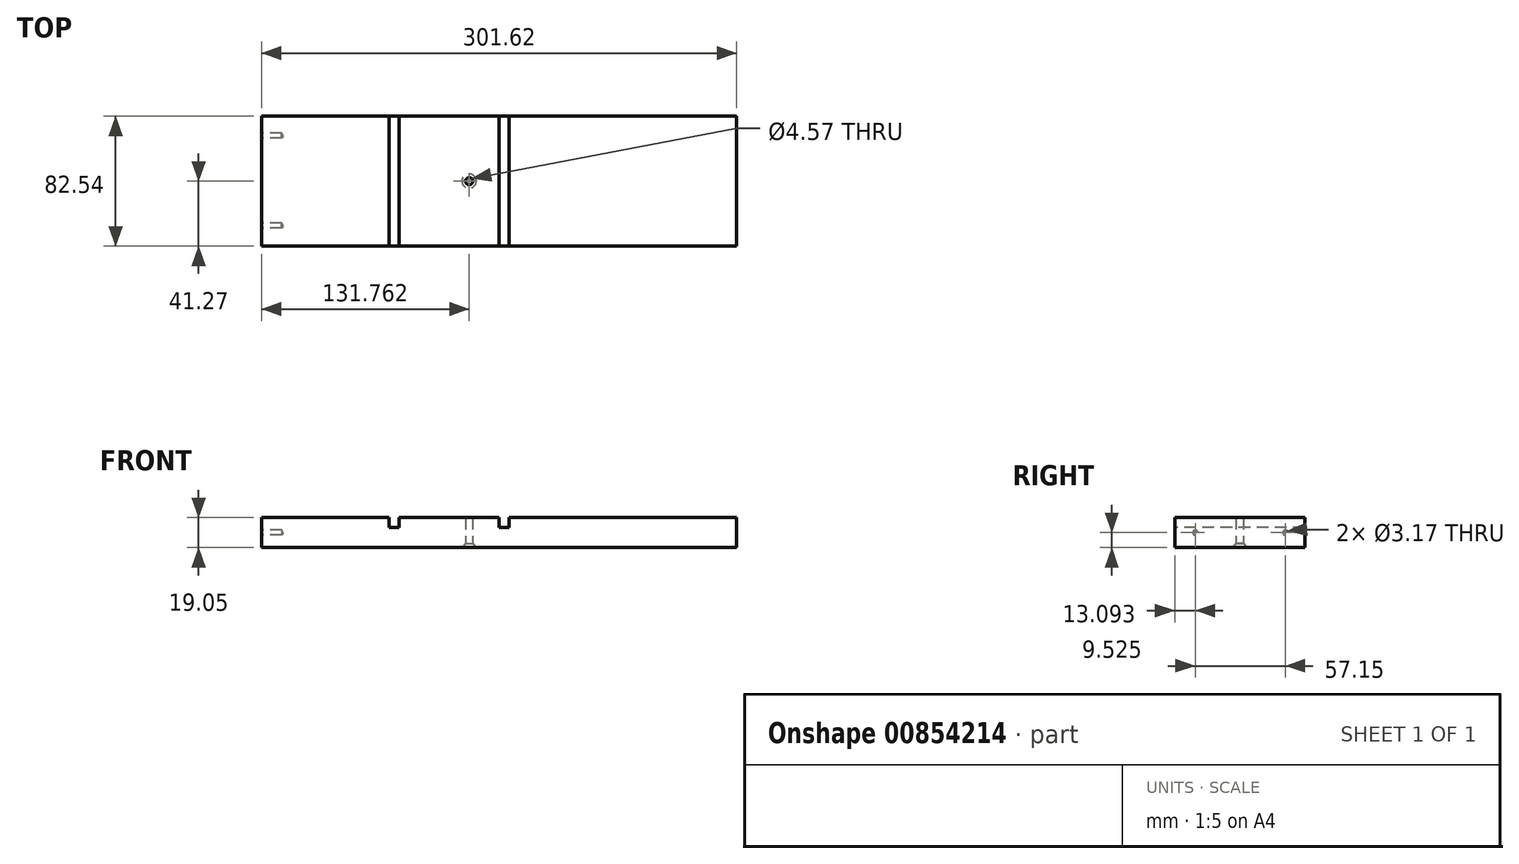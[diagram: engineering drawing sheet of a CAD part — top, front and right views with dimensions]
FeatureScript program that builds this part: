
annotation { "Feature Type Name" : "Feature", "Feature Type Description" : "" }
export const myFeature = defineFeature(function(context is Context, id is Id, definition is map)
    precondition{}
    {
        {
            var Q0;
            Q0=qCreatedBy(makeId("Top.planeOp"),FACE);
            var sketch = newSketch(context, id + "F0", { "sketchPlane" : qUnion([Q0])});
            skLineSegment(sketch, "E0", {"start": v(-114.3, 41.27) * mm, "end": v(187.33, 41.28) * mm});
            skLineSegment(sketch, "E1", {"start": v(-114.3, 41.27) * mm, "end": v(-114.3, -41.28) * mm});
            skLineSegment(sketch, "E2", {"start": v(-114.3, -41.27) * mm, "end": v(187.32, -41.27) * mm});
            skLineSegment(sketch, "E3", {"start": v(187.32, -41.28) * mm, "end": v(187.32, 41.28) * mm});
            skLineSegment(sketch, "E4", {"start": v(187.33, 41.28) * mm, "end": v(187.32, 41.28) * mm});
            skSolve(sketch);
        }
        {
            var Q0;
            Q0=makeQuery(id+"F0.imprint","IMPRINT",FACE,{"disambiguationData":[TD([[makeQuery(id+"F0.imprint","IMPRINT",EDGE,{"derivedFrom":sQuery(id+"F0.wireOp",EDGE,"E0")}),-1.0]])]});
            extrude(context, id + "F1", {"entities" : qUnion([Q0]), "depth" : 19.05 * mm, "offsetDistance" : 25.4 * mm});
        }
        {
            var Q0;
            Q0=makeQuery(id+"F1.opExtrude","CAP_FACE",FACE,{"disambiguationData":[OSD([sQuery(id+"F0.wireOp",EDGE,"E0"),sQuery(id+"F0.wireOp",EDGE,"E1"),sQuery(id+"F0.wireOp",EDGE,"E2"),sQuery(id+"F0.wireOp",EDGE,"E3")])],"isStart":false});
            var sketch = newSketch(context, id + "F2", { "sketchPlane" : qUnion([Q0])});
            skLineSegment(sketch, "E5", {"start": v(-33.34, 41.27) * mm, "end": v(-33.34, -41.27) * mm});
            skLineSegment(sketch, "E6", {"start": v(-26.99, 41.27) * mm, "end": v(-26.99, -41.27) * mm});
            skLineSegment(sketch, "E7", {"start": v(36.51, 41.28) * mm, "end": v(36.51, -41.27) * mm});
            skLineSegment(sketch, "E8", {"start": v(42.86, -41.27) * mm, "end": v(42.86, 41.28) * mm});
            skCircle(sketch, "E9", {"center": v(24.49, 0) * mm, "radius": 2.38 * mm});
            skPoint(sketch, "E9.centerSnap0", {"position": v(36.51, 0) * mm});
            skSolve(sketch);
        }
        {
            var Q0;
            {var subQ0=sQuery(id+"F2.wireOp",EDGE,"E5");Q0=makeQuery(id+"F2.imprint","IMPRINT",FACE,{"disambiguationData":[TD([[makeQuery(id+"F2.imprint","IMPRINT",EDGE,{"derivedFrom":subQ0}),1.0]])]});}
            var Q1;
            {var subQ0=sQuery(id+"F2.wireOp",EDGE,"E7");Q1=makeQuery(id+"F2.imprint","IMPRINT",FACE,{"disambiguationData":[TD([[makeQuery(id+"F2.imprint","IMPRINT",EDGE,{"derivedFrom":subQ0}),1.0]])]});}
            extrude(context, id + "F3", {"entities" : qUnion([Q0, Q1]), "operationType" : NewBodyOperationType.REMOVE, "oppositeDirection" : true, "depth" : 6.35 * mm, "offsetDistance" : 25.4 * mm});
        }
        {
            var Q0;
            Q0=makeQuery(id+"F1.opExtrude","CAP_FACE",FACE,{"disambiguationData":[OSD([sQuery(id+"F0.wireOp",EDGE,"E0"),sQuery(id+"F0.wireOp",EDGE,"E1"),sQuery(id+"F0.wireOp",EDGE,"E2"),sQuery(id+"F0.wireOp",EDGE,"E3")])],"isStart":true});
            var sketch = newSketch(context, id + "F4", { "sketchPlane" : qUnion([Q0])});
            skPoint(sketch, "E10", {"position": v(17.46, 0) * mm});
            skSolve(sketch);
        }
        {
            var Q0;
            Q0=sQuery(id+"F4.wireOp",VERTEX,"E10");
            var Q1;
            Q1=makeQuery(id+"F1.opExtrude","SWEPT_BODY",BODY,{"disambiguationData":[OSD([sQuery(id+"F0.wireOp",EDGE,"E0"),sQuery(id+"F0.wireOp",EDGE,"E1"),sQuery(id+"F0.wireOp",EDGE,"E2"),sQuery(id+"F0.wireOp",EDGE,"E3")])]});
            hole(context, id + "F5", {"style" : HoleStyle.C_SINK, "endStyle" : HoleEndStyle.THROUGH, "standardTappedOrClearance" : lookupTablePath({ "fit" : "Close (ASME)", "standard" : "ANSI", "size" : "#8", "type" : "Clearance" }), "standardBlindInLast" : lookupTablePath({ "fit" : "Close", "standard" : "ANSI", "size" : "#8", "type" : "Clearance" }), "holeDiameter" : 4.57 * mm, "cSinkDiameter" : 9.12 * mm, "cSinkAngle" : 82 * degree, "majorDiameter" : 6.35 * mm, "isTappedThrough" : true, "tappedDepth" : 12.7 * mm, "tapClearance" : 3, "startFromSketch" : true, "locations" : qUnion([Q0]), "scope" : qUnion([Q1])});
        }
        {
            var Q0;
            Q0=makeQuery(id+"F1.opExtrude","SWEPT_FACE",FACE,{"disambiguationData":[OSD([sQuery(id+"F0.wireOp",EDGE,"E1")])]});
            var sketch = newSketch(context, id + "F6", { "sketchPlane" : qUnion([Q0])});
            skPoint(sketch, "E11", {"position": v(-28.97, 9.52) * mm});
            skPoint(sketch, "E12", {"position": v(28.18, 9.53) * mm});
            skSolve(sketch);
        }
        {
            var Q0;
            Q0=sQuery(id+"F6.wireOp",VERTEX,"E11");
            var Q1;
            Q1=sQuery(id+"F6.wireOp",VERTEX,"E12");
            var Q2;
            Q2=makeQuery(id+"F1.opExtrude","SWEPT_BODY",BODY,{"disambiguationData":[OSD([sQuery(id+"F0.wireOp",EDGE,"E0"),sQuery(id+"F0.wireOp",EDGE,"E1"),sQuery(id+"F0.wireOp",EDGE,"E2"),sQuery(id+"F0.wireOp",EDGE,"E3")])]});
            hole(context, id + "F7", {"style" : HoleStyle.SIMPLE, "endStyle" : HoleEndStyle.BLIND, "holeDiameter" : 3.17 * mm, "majorDiameter" : 6.35 * mm, "holeDepth" : 12.7 * mm, "isTappedThrough" : true, "tappedDepth" : 12.7 * mm, "tapClearance" : 3, "startFromSketch" : true, "locations" : qUnion([Q0, Q1]), "scope" : qUnion([Q2])});
        }
    });
